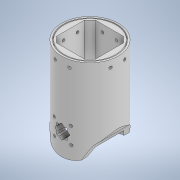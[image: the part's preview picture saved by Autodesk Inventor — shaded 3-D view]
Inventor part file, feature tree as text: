
AUTODESK INVENTOR PART (.ipt)
format: ipt  version: 2021 (Build 250183000, 183)  size: 288,256 bytes
history: native  units: mm
features: extrude x8, sketch x8
ambient origin geometry x8: Origin, YZ Plane, XZ Plane, XY Plane, X Axis, Y Axis, Z Axis, Center Point
bodies: Body1 (feature_tree)
feature tree (16):
  extrude  "Extrusión2"  Depth=100.0mm TaperAngle=0.0deg
  sketch  "Boceto5"  dims[d45=100.0mm d46=0.0mm d53=10.0mm]
  sketch  "Boceto6"  dims[d54=10.0mm d55=25.0mm]
  sketch  "Boceto7"  dims[d58=20.0mm d59=20.0mm]
  extrude  "Extrusión4"  Depth=10.0mm
  extrude  "Extrusión8"  Depth=10.0mm
  extrude  "Extrusión10"  Depth=20.0mm
  extrude  "Extrusión12"  Depth=30.0mm
  extrude  "Extrusión13"  Depth=200.0mm TaperAngle=0.0deg
  extrude  "Extrusión14"  Depth=8.0mm
  extrude  "Extrusión15"  Depth=8.0mm
  sketch  "Boceto4"  dims[d20=40.0mm d22=360.0deg d28=100.0mm d29=0.0mm]
  sketch  "Boceto10"  dims[d60=30.0mm d61=30.0mm]
  sketch  "Boceto11"  dims[d62=200.0mm d63=0.0mm d77=200.0mm d78=0.0mm]
  sketch  "Boceto12"  dims[d95=8.0mm d96=8.0mm]
  sketch  "Boceto13"  dims[d97=3.0mm d98=8.0mm d99=8.0mm d100=3.0mm d101=200.0mm d102=0.0mm d111=200.0mm d112=0.0mm d113=59.0mm d114=61.0mm d115=2.5mm d116=0.0mm d119=40.0mm d121=360.0deg d123=200.0mm d124=0.0mm d11=0.5mm d12=0.872665mm d13=0.5mm d14=0.872665mm d30=0.5mm d31=0.872665mm d36=0.5mm d37=0.872665mm d38=0.5mm d39=0.872665mm d47=0.5mm d48=0.872665mm d49=0.5mm d50=0.872665mm d68=0.5mm d69=0.872665mm d70=0.5mm d71=0.872665mm]
